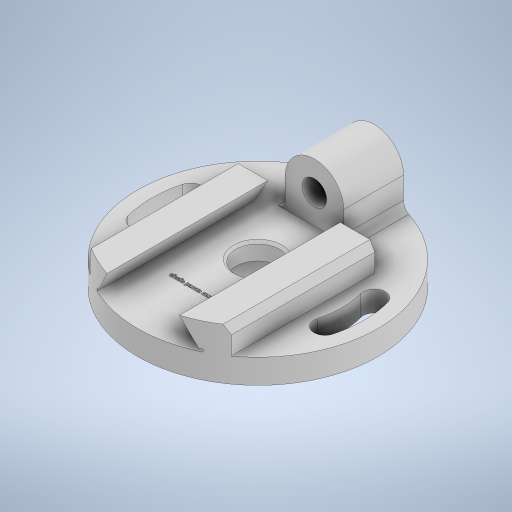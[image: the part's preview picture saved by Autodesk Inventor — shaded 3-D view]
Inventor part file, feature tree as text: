
AUTODESK INVENTOR PART (.ipt)
format: ipt  version: 2023 (Build 270158000, 158)  size: 690,176 bytes
history: native  units: mm
features: extrude x6, sketch x4, chamfer x3, revolve x1, mirror x1, fillet x1
ambient origin geometry x8: Origin, YZ Plane, XZ Plane, XY Plane, X Axis, Y Axis, Z Axis, Center Point
bodies: Solido1 (feature_tree)
feature tree (16):
  sketch  "Schizzo1"
  revolve  "Rivoluzione1"
  extrude  "Estrusione1"  Depth=197.0mm
  extrude  "Estrusione2"  Depth=185.0mm
  mirror  "Specchio1"
  sketch  "Schizzo2"
  extrude  "Estrusione3"  Depth=116.0mm
  extrude  "Estrusione4"  Depth=88.0mm
  extrude  "Estrusione5"  Depth=67.0mm
  fillet  "Raccordo1"  Radius=58.0mm
  chamfer  "Smusso1"  Distance=87.0mm
  chamfer  "Smusso2"  Distance=36.0mm
  chamfer  "Smusso3"  Distance=12.0mm
  extrude  "Estrusione6"  Depth=64.0mm
  sketch  "Schizzo3"
  sketch  "Schizzo4"
